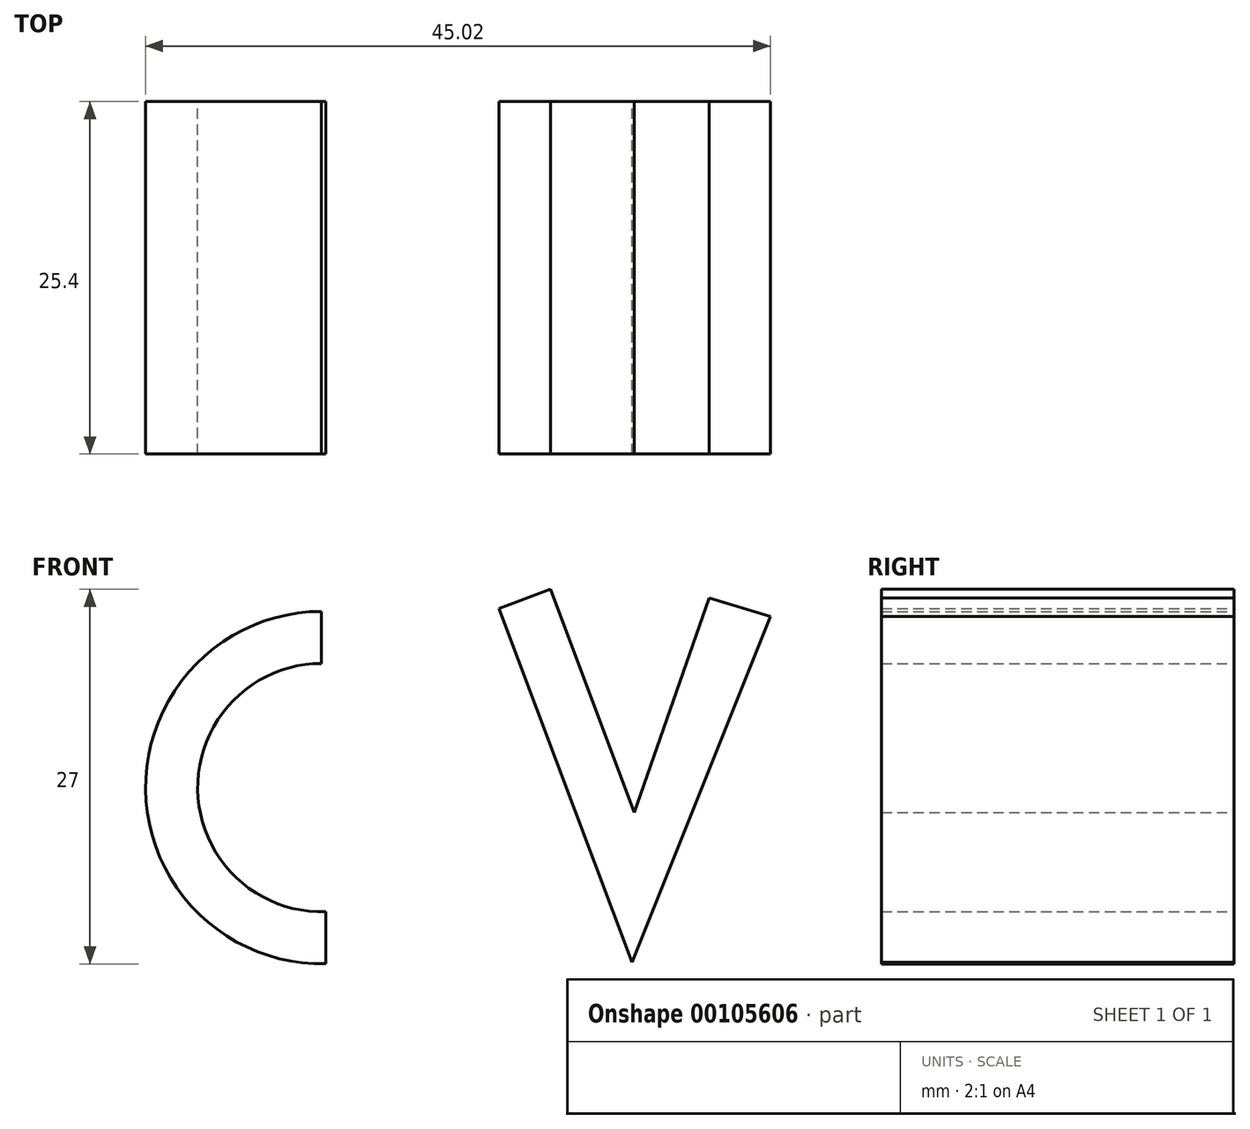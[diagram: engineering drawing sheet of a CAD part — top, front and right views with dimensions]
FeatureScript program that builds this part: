
annotation { "Feature Type Name" : "Feature", "Feature Type Description" : "" }
export const myFeature = defineFeature(function(context is Context, id is Id, definition is map)
    precondition{}
    {
        {
            var Q0;
            Q0=qCreatedBy(makeId("Front.planeOp"),FACE);
            var sketch = newSketch(context, id + "F0", { "sketchPlane" : qUnion([Q0])});
            skArc(sketch, "E0", {"start": v(-61.96, 47.6) * mm, "mid": v(-74.63, 34.75) * mm, "end": v(-61.65, 22.2) * mm});
            skLineSegment(sketch, "E1", {"start": v(-49.16, 47.81) * mm, "end": v(-39.57, 22.33) * mm});
            skLineSegment(sketch, "E2", {"start": v(-39.57, 22.33) * mm, "end": v(-29.6, 47.24) * mm});
            skArc(sketch, "E3", {"start": v(-61.96, 43.85) * mm, "mid": v(-70.88, 34.75) * mm, "end": v(-61.65, 25.96) * mm});
            skLineSegment(sketch, "E4", {"start": v(-61.96, 47.6) * mm, "end": v(-61.96, 43.85) * mm});
            skLineSegment(sketch, "E5", {"start": v(-61.65, 25.96) * mm, "end": v(-61.65, 22.2) * mm});
            skLineSegment(sketch, "E6", {"start": v(-49.16, 47.81) * mm, "end": v(-45.46, 49.2) * mm});
            skLineSegment(sketch, "E7", {"start": v(-45.46, 49.2) * mm, "end": v(-39.4, 33.1) * mm});
            skLineSegment(sketch, "E8", {"start": v(-39.4, 33.1) * mm, "end": v(-34.02, 48.58) * mm});
            skLineSegment(sketch, "E9", {"start": v(-34.02, 48.58) * mm, "end": v(-29.6, 47.24) * mm});
            skSolve(sketch);
        }
        {
            var Q0;
            Q0 = qSketchRegion(id + "F0", true);
            extrude(context, id + "F1", {"entities" : qUnion([Q0]), "depth" : 25.4 * mm});
        }
    });
